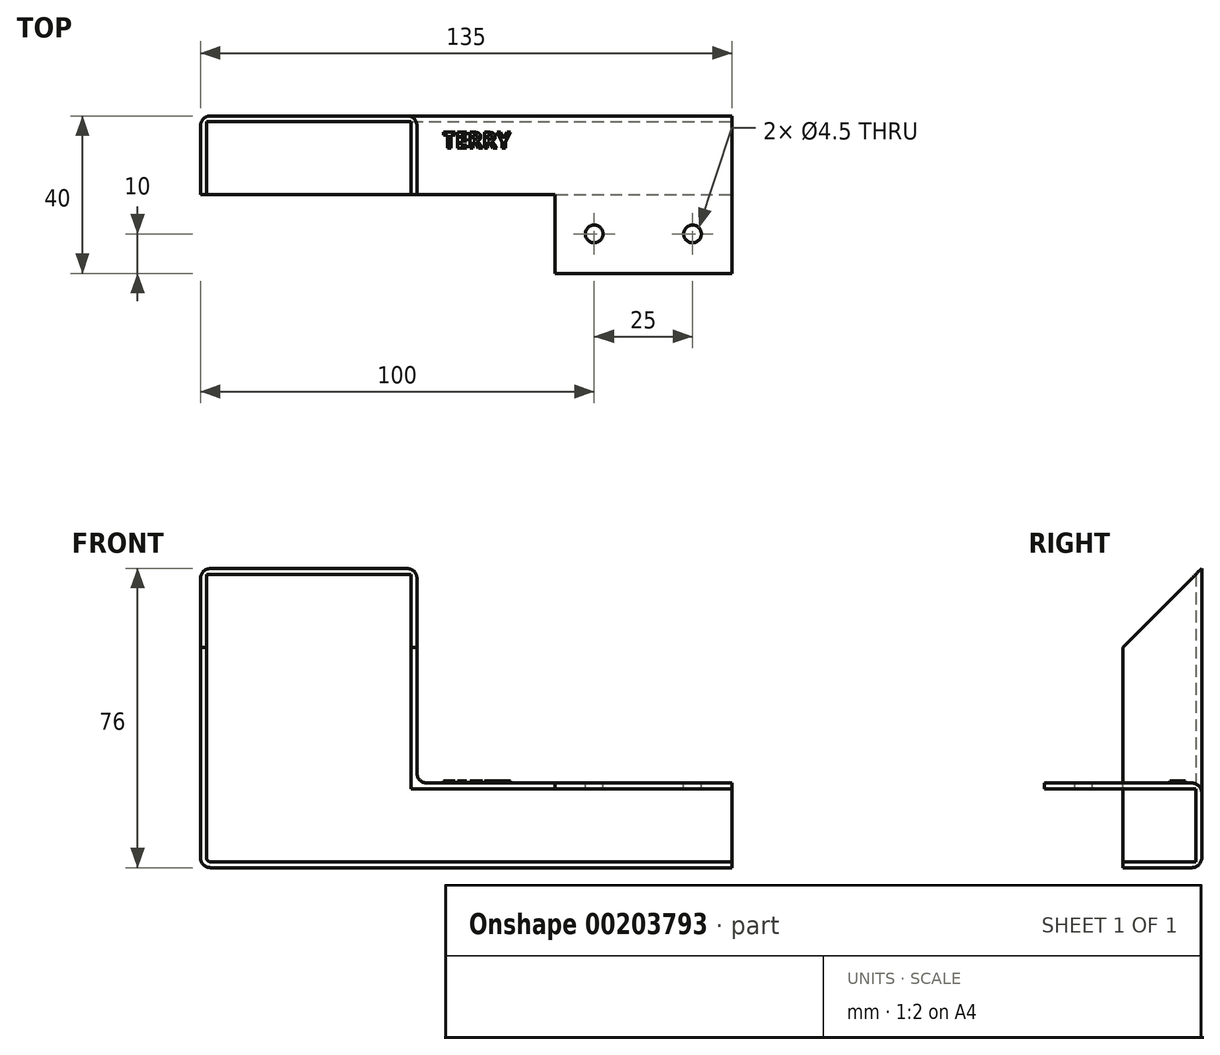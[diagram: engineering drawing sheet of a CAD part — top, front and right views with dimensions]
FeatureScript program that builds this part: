
annotation { "Feature Type Name" : "Feature", "Feature Type Description" : "" }
export const myFeature = defineFeature(function(context is Context, id is Id, definition is map)
    precondition{}
    {
        {
            var Q0;
            Q0=qCreatedBy(makeId("Front.planeOp"),FACE);
            var sketch = newSketch(context, id + "F0", { "sketchPlane" : qUnion([Q0])});
            skLineSegment(sketch, "E0", {"start": v(0, 0) * mm, "end": v(80, 0) * mm});
            skLineSegment(sketch, "E1", {"start": v(80, 0) * mm, "end": v(80, -21.5) * mm});
            skLineSegment(sketch, "E2", {"start": v(80, -21.5) * mm, "end": v(-55, -21.5) * mm});
            skLineSegment(sketch, "E3", {"start": v(-55, -21.5) * mm, "end": v(-55, 54.5) * mm});
            skLineSegment(sketch, "E4", {"start": v(-55, 54.5) * mm, "end": v(0, 54.5) * mm});
            skLineSegment(sketch, "E5", {"start": v(0, 54.5) * mm, "end": v(0, 0) * mm});
            skSolve(sketch);
        }
        {
            var Q0;
            Q0=makeQuery(id+"F0.imprint","IMPRINT",FACE,{"disambiguationData":[TD([[makeQuery(id+"F0.imprint","IMPRINT",EDGE,{"derivedFrom":sQuery(id+"F0.wireOp",EDGE,"E0")}),-1.0]])]});
            extrude(context, id + "F1", {"entities" : qUnion([Q0]), "depth" : 1.5 * mm});
        }
        {
            var Q0;
            Q0=makeQuery(id+"F1.opExtrude","CAP_FACE",FACE,{"disambiguationData":[OSD([sQuery(id+"F0.wireOp",EDGE,"E0"),sQuery(id+"F0.wireOp",EDGE,"E1"),sQuery(id+"F0.wireOp",EDGE,"E2"),sQuery(id+"F0.wireOp",EDGE,"E3"),sQuery(id+"F0.wireOp",EDGE,"E4"),sQuery(id+"F0.wireOp",EDGE,"E5")])],"isStart":false});
            var sketch = newSketch(context, id + "F2", { "sketchPlane" : qUnion([Q0])});
            skLineSegment(sketch, "E6", {"start": v(-55, 54.5) * mm, "end": v(-55, -21.5) * mm});
            skLineSegment(sketch, "E7", {"start": v(-55, -21.5) * mm, "end": v(80, -21.5) * mm});
            skLineSegment(sketch, "E8", {"start": v(80, 0) * mm, "end": v(0, 0) * mm});
            skLineSegment(sketch, "E9", {"start": v(0, 0) * mm, "end": v(0, 54.5) * mm});
            skLineSegment(sketch, "E10.0", {"start": v(-53.5, -20) * mm, "end": v(80, -20) * mm});
            skLineSegment(sketch, "E10.1", {"start": v(-53.5, 54.5) * mm, "end": v(-53.5, -20) * mm});
            skLineSegment(sketch, "E11.0", {"start": v(-1.5, -1.5) * mm, "end": v(-1.5, 54.5) * mm});
            skLineSegment(sketch, "E11.1", {"start": v(80, -1.5) * mm, "end": v(-1.5, -1.5) * mm});
            skSolve(sketch);
        }
        {
            var Q0;
            {var subQ1=sQuery(id+"F2.wireOp",EDGE,"E6");Q0=makeQuery(id+"F2.imprint","IMPRINT",FACE,{"disambiguationData":[TD([[makeQuery(id+"F2.imprint","IMPRINT",EDGE,{"derivedFrom":subQ1}),-1.0]])]});}
            var Q1;
            {var subQ3=sQuery(id+"F2.wireOp",EDGE,"E8");Q1=makeQuery(id+"F2.imprint","IMPRINT",FACE,{"disambiguationData":[TD([[makeQuery(id+"F2.imprint","IMPRINT",EDGE,{"derivedFrom":subQ3}),-1.0]])]});}
            extrude(context, id + "F3", {"entities" : qUnion([Q0, Q1]), "operationType" : NewBodyOperationType.ADD, "depth" : 18.5 * mm});
        }
        {
            var Q0;
            Q0=makeQuery(id+"F3.opExtrude","CAP_FACE",FACE,{"disambiguationData":[OSD([sQuery(id+"F0.wireOp",EDGE,"E1"),sQuery(id+"F0.wireOp",EDGE,"E4"),sQuery(id+"F2.wireOp",EDGE,"E8"),sQuery(id+"F2.wireOp",EDGE,"E9"),sQuery(id+"F2.wireOp",EDGE,"E11.0"),sQuery(id+"F2.wireOp",EDGE,"E11.1")])],"isStart":false});
            var sketch = newSketch(context, id + "F4", { "sketchPlane" : qUnion([Q0])});
            skLineSegment(sketch, "E12", {"start": v(80, 0) * mm, "end": v(80, -1.5) * mm});
            skLineSegment(sketch, "E13", {"start": v(80, -1.5) * mm, "end": v(35, -1.5) * mm});
            skLineSegment(sketch, "E14", {"start": v(35, -1.5) * mm, "end": v(35, 0) * mm});
            skPoint(sketch, "E14.endSnap0", {"position": v(40, 0) * mm});
            skLineSegment(sketch, "E15", {"start": v(35, 0) * mm, "end": v(80, 0) * mm});
            skSolve(sketch);
        }
        {
            var Q0;
            Q0=makeQuery(id+"F4.imprint","IMPRINT",FACE,{"disambiguationData":[TD([[makeQuery(id+"F4.imprint","IMPRINT",EDGE,{"derivedFrom":sQuery(id+"F4.wireOp",EDGE,"E12")}),-1.0]])]});
            extrude(context, id + "F5", {"entities" : qUnion([Q0]), "operationType" : NewBodyOperationType.ADD, "depth" : 20 * mm});
        }
        {
            var Q0;
            Q0=makeQuery(id+"F5.boolean.opBoolean","MERGE",FACE,{"derivedFrom":[makeQuery(id+"F3.boolean.opBoolean","MERGE",FACE,{"derivedFrom":[makeQuery(id+"F1.opExtrude","SWEPT_FACE",FACE,{"disambiguationData":[OSD([sQuery(id+"F0.wireOp",EDGE,"E0")])]}),makeQuery(id+"F3.opExtrude","SWEPT_FACE",FACE,{"disambiguationData":[OSD([sQuery(id+"F2.wireOp",EDGE,"E8")])]})]}),makeQuery(id+"F5.opExtrude","SWEPT_FACE",FACE,{"disambiguationData":[OSD([sQuery(id+"F4.wireOp",EDGE,"E15")])]})]});
            var sketch = newSketch(context, id + "F6", { "sketchPlane" : qUnion([Q0])});
            skLineSegment(sketch, "E16", {"start": v(80, -40) * mm, "end": v(80, -30) * mm, "construction": true});
            skLineSegment(sketch, "E17", {"start": v(80, -30) * mm, "end": v(70, -30) * mm, "construction": true});
            skLineSegment(sketch, "E18", {"start": v(70, -30) * mm, "end": v(45, -30) * mm, "construction": true});
            skCircle(sketch, "E19", {"center": v(45, -30) * mm, "radius": 2.25 * mm});
            skCircle(sketch, "E20", {"center": v(70, -30) * mm, "radius": 2.25 * mm});
            skSolve(sketch);
        }
        {
            var Q0;
            Q0=makeQuery(id+"F6.imprint","IMPRINT",FACE,{"disambiguationData":[TD([[makeQuery(id+"F6.imprint","IMPRINT",EDGE,{"derivedFrom":sQuery(id+"F6.wireOp",EDGE,"E19")}),1.0]])]});
            var Q1;
            Q1=makeQuery(id+"F6.imprint","IMPRINT",FACE,{"disambiguationData":[TD([[makeQuery(id+"F6.imprint","IMPRINT",EDGE,{"derivedFrom":sQuery(id+"F6.wireOp",EDGE,"E20")}),1.0]])]});
            extrude(context, id + "F7", {"entities" : qUnion([Q0, Q1]), "operationType" : NewBodyOperationType.REMOVE, "endBound" : BoundingType.UP_TO_NEXT, "oppositeDirection" : true, "depth" : 25 * mm});
        }
        {
            var Q0;
            Q0=makeQuery(id+"F3.boolean.opBoolean","MERGE",FACE,{"derivedFrom":[makeQuery(id+"F1.opExtrude","SWEPT_FACE",FACE,{"disambiguationData":[OSD([sQuery(id+"F0.wireOp",EDGE,"E3")])]}),makeQuery(id+"F3.opExtrude","SWEPT_FACE",FACE,{"disambiguationData":[OSD([sQuery(id+"F2.wireOp",EDGE,"E6")])]})]});
            var sketch = newSketch(context, id + "F8", { "sketchPlane" : qUnion([Q0])});
            skLineSegment(sketch, "E21", {"start": v(0, 54.5) * mm, "end": v(0, 34.5) * mm, "construction": true});
            skLineSegment(sketch, "E22", {"start": v(0, 34.5) * mm, "end": v(20, 34.5) * mm, "construction": true});
            skLineSegment(sketch, "E23", {"start": v(20, 34.5) * mm, "end": v(0, 54.5) * mm});
            skLineSegment(sketch, "E24", {"start": v(20, 54.5) * mm, "end": v(20, 34.5) * mm});
            skSolve(sketch);
        }
        {
            var Q0;
            Q0=makeQuery(id+"F8.imprint","IMPRINT",FACE,{"disambiguationData":[TD([[makeQuery(id+"F8.imprint","IMPRINT",EDGE,{"derivedFrom":sQuery(id+"F8.wireOp",EDGE,"E23")}),-1.0]])]});
            extrude(context, id + "F9", {"entities" : qUnion([Q0]), "operationType" : NewBodyOperationType.REMOVE, "oppositeDirection" : true, "depth" : 55 * mm});
        }
        {
            var Q0;
            Q0=makeQuery(id+"F3.opExtrude","CAP_EDGE",EDGE,{"disambiguationData":[OSD([sQuery(id+"F2.wireOp",EDGE,"E11.0")])],"isStart":true});
            var Q1;
            Q1=makeQuery(id+"F3.opExtrude","CAP_EDGE",EDGE,{"disambiguationData":[OSD([sQuery(id+"F2.wireOp",EDGE,"E10.0")])],"isStart":true});
            var Q2;
            Q2=makeQuery(id+"F3.opExtrude","CAP_EDGE",EDGE,{"disambiguationData":[OSD([sQuery(id+"F2.wireOp",EDGE,"E10.1")])],"isStart":true});
            var Q3;
            Q3=makeQuery(id+"F3.opExtrude","SWEPT_EDGE",EDGE,{"disambiguationData":[OSD([sQuery(id+"F2.wireOp",EDGE,"E10.0"),sQuery(id+"F2.wireOp",EDGE,"E10.1")])]});
            fillet(context, id + "F10", {"entities" : qUnion([Q0, Q1, Q2, Q3]), "radius" : 1 * mm, "tangentPropagation" : true, "allowEdgeOverflow" : false});
        }
        {
            var Q0;
            Q0=makeQuery(id+"F1.opExtrude","CAP_EDGE",EDGE,{"disambiguationData":[OSD([sQuery(id+"F0.wireOp",EDGE,"E2")])],"isStart":true});
            var Q1;
            Q1=makeQuery(id+"F1.opExtrude","CAP_EDGE",EDGE,{"disambiguationData":[OSD([sQuery(id+"F0.wireOp",EDGE,"E0")])],"isStart":true});
            var Q2;
            Q2=makeQuery(id+"F1.opExtrude","CAP_EDGE",EDGE,{"disambiguationData":[OSD([sQuery(id+"F0.wireOp",EDGE,"E5")])],"isStart":true});
            var Q3;
            Q3=makeQuery(id+"F1.opExtrude","CAP_EDGE",EDGE,{"disambiguationData":[OSD([sQuery(id+"F0.wireOp",EDGE,"E3")])],"isStart":true});
            var Q4;
            Q4=makeQuery(id+"F3.boolean.opBoolean","MERGE",EDGE,{"derivedFrom":[makeQuery(id+"F1.opExtrude","SWEPT_EDGE",EDGE,{"disambiguationData":[OSD([sQuery(id+"F0.wireOp",EDGE,"E2"),sQuery(id+"F0.wireOp",EDGE,"E3")])]}),makeQuery(id+"F3.opExtrude","SWEPT_EDGE",EDGE,{"disambiguationData":[OSD([sQuery(id+"F2.wireOp",EDGE,"E6"),sQuery(id+"F2.wireOp",EDGE,"E7")])]})]});
            var Q5;
            Q5=makeQuery(id+"F3.boolean.opBoolean","MERGE",EDGE,{"derivedFrom":[makeQuery(id+"F1.opExtrude","SWEPT_EDGE",EDGE,{"disambiguationData":[OSD([sQuery(id+"F0.wireOp",EDGE,"E0"),sQuery(id+"F0.wireOp",EDGE,"E5")])]}),makeQuery(id+"F3.opExtrude","SWEPT_EDGE",EDGE,{"disambiguationData":[OSD([sQuery(id+"F2.wireOp",EDGE,"E8"),sQuery(id+"F2.wireOp",EDGE,"E9")])]})]});
            fillet(context, id + "F11", {"entities" : qUnion([Q0, Q1, Q2, Q3, Q4, Q5]), "radius" : 2.5 * mm, "tangentPropagation" : true, "allowEdgeOverflow" : false});
        }
        {
            var Q0;
            Q0=makeQuery(id+"F5.boolean.opBoolean","MERGE",FACE,{"derivedFrom":[makeQuery(id+"F3.boolean.opBoolean","MERGE",FACE,{"derivedFrom":[makeQuery(id+"F1.opExtrude","SWEPT_FACE",FACE,{"disambiguationData":[OSD([sQuery(id+"F0.wireOp",EDGE,"E0")])]}),makeQuery(id+"F3.opExtrude","SWEPT_FACE",FACE,{"disambiguationData":[OSD([sQuery(id+"F2.wireOp",EDGE,"E8")])]})]}),makeQuery(id+"F5.opExtrude","SWEPT_FACE",FACE,{"disambiguationData":[OSD([sQuery(id+"F4.wireOp",EDGE,"E15")])]})]});
            var sketch = newSketch(context, id + "F12", { "sketchPlane" : qUnion([Q0])});
            skText(sketch, "E25", { "text": "TERRY", "fontName": "OpenSans-Bold.ttf"});
            const initialGuessF12  = {"E25": [0.00662, -0.00813, 1, 0, 0.004]};
            skSetInitialGuess(sketch, initialGuessF12);
            skSolve(sketch);
        }
        {
            var Q0;
            Q0 = qSketchRegion(id + "F12", true);
            extrude(context, id + "F13", {"entities" : qUnion([Q0]), "operationType" : NewBodyOperationType.ADD, "depth" : 0.5 * mm});
        }
    });
